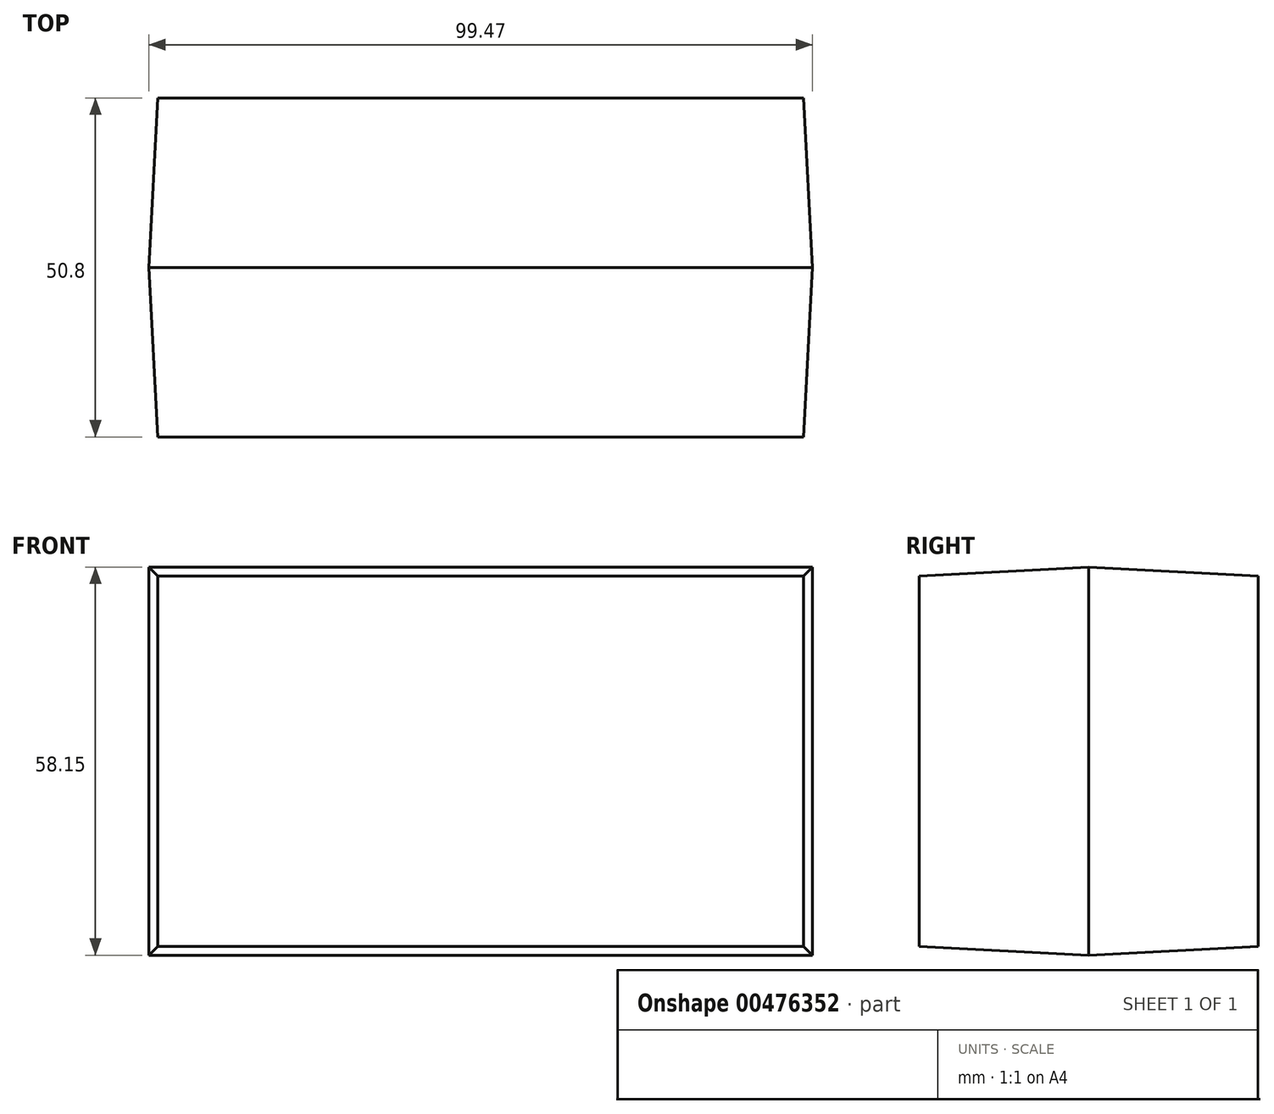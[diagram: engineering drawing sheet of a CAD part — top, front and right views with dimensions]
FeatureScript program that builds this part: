
annotation { "Feature Type Name" : "Feature", "Feature Type Description" : "" }
export const myFeature = defineFeature(function(context is Context, id is Id, definition is map)
    precondition{}
    {
        {
            var Q0;
            Q0=qCreatedBy(makeId("Front.planeOp"),FACE);
            var sketch = newSketch(context, id + "F0", { "sketchPlane" : qUnion([Q0])});
            skLineSegment(sketch, "E0.bottom", {"start": v(0, 0) * mm, "end": v(99.47, 0) * mm});
            skLineSegment(sketch, "E0.top", {"start": v(0, 58.15) * mm, "end": v(99.47, 58.15) * mm});
            skLineSegment(sketch, "E0.left", {"start": v(0, 0) * mm, "end": v(0, 58.15) * mm});
            skLineSegment(sketch, "E0.right", {"start": v(99.47, 0) * mm, "end": v(99.47, 58.15) * mm});
            skSolve(sketch);
        }
        {
            var Q0;
            Q0=makeQuery(id+"F0.imprint","IMPRINT",FACE,{"disambiguationData":[TD([[makeQuery(id+"F0.imprint","IMPRINT",EDGE,{"derivedFrom":sQuery(id+"F0.wireOp",EDGE,"E0.bottom")}),1.0]])]});
            extrude(context, id + "F1", {"entities" : qUnion([Q0]), "endBound" : BoundingType.SYMMETRIC, "oppositeDirection" : true, "depth" : 50.8 * mm, "hasDraft" : true, "draftAngle" : 3 * degree, "draftPullDirection" : true});
        }
    });
